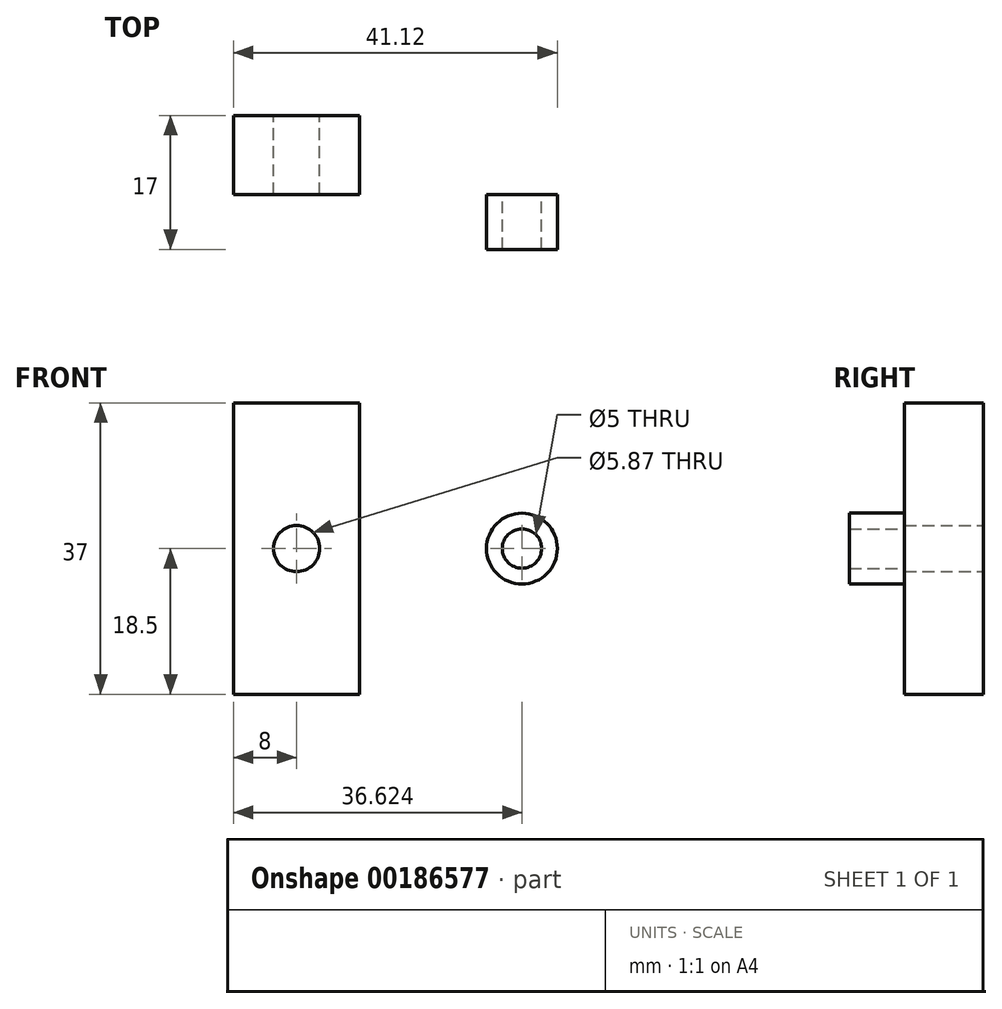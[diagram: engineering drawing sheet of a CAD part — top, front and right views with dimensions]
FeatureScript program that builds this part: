
annotation { "Feature Type Name" : "Feature", "Feature Type Description" : "" }
export const myFeature = defineFeature(function(context is Context, id is Id, definition is map)
    precondition{}
    {
        {
            var Q0;
            Q0=qCreatedBy(makeId("Front.planeOp"),FACE);
            var sketch = newSketch(context, id + "F0", { "sketchPlane" : qUnion([Q0])});
            skLineSegment(sketch, "E0.bottom", {"start": v(8, 18.5) * mm, "end": v(-8, 18.5) * mm});
            skLineSegment(sketch, "E0.top", {"start": v(8, -18.5) * mm, "end": v(-8, -18.5) * mm});
            skLineSegment(sketch, "E0.left", {"start": v(8, 18.5) * mm, "end": v(8, -18.5) * mm});
            skLineSegment(sketch, "E0.right", {"start": v(-8, 18.5) * mm, "end": v(-8, -18.5) * mm});
            skPoint(sketch, "E0.middle", {"position": v(0, 0) * mm});
            skCircle(sketch, "E1", {"center": v(0, 0) * mm, "radius": 2.93 * mm});
            skSolve(sketch);
        }
        {
            var Q0;
            Q0 = qSketchRegion(id + "F0", true);
            extrude(context, id + "F1", {"entities" : qUnion([Q0]), "depth" : 10 * mm});
        }
        {
            var Q0;
            Q0=makeQuery(id+"F1.opExtrude","CAP_FACE",FACE,{"disambiguationData":[OSD([sQuery(id+"F0.wireOp",EDGE,"E0.bottom"),sQuery(id+"F0.wireOp",EDGE,"E0.top"),sQuery(id+"F0.wireOp",EDGE,"E0.left"),sQuery(id+"F0.wireOp",EDGE,"E0.right"),sQuery(id+"F0.wireOp",EDGE,"E1")])],"isStart":false});
            var sketch = newSketch(context, id + "F2", { "sketchPlane" : qUnion([Q0])});
            skCircle(sketch, "E2", {"center": v(28.62, 0) * mm, "radius": 2.5 * mm});
            skCircle(sketch, "E3", {"center": v(28.62, 0) * mm, "radius": 4.5 * mm});
            skSolve(sketch);
        }
        {
            var Q0;
            Q0 = qSketchRegion(id + "F2", true);
            extrude(context, id + "F3", {"entities" : qUnion([Q0]), "depth" : 7 * mm});
        }
    });
